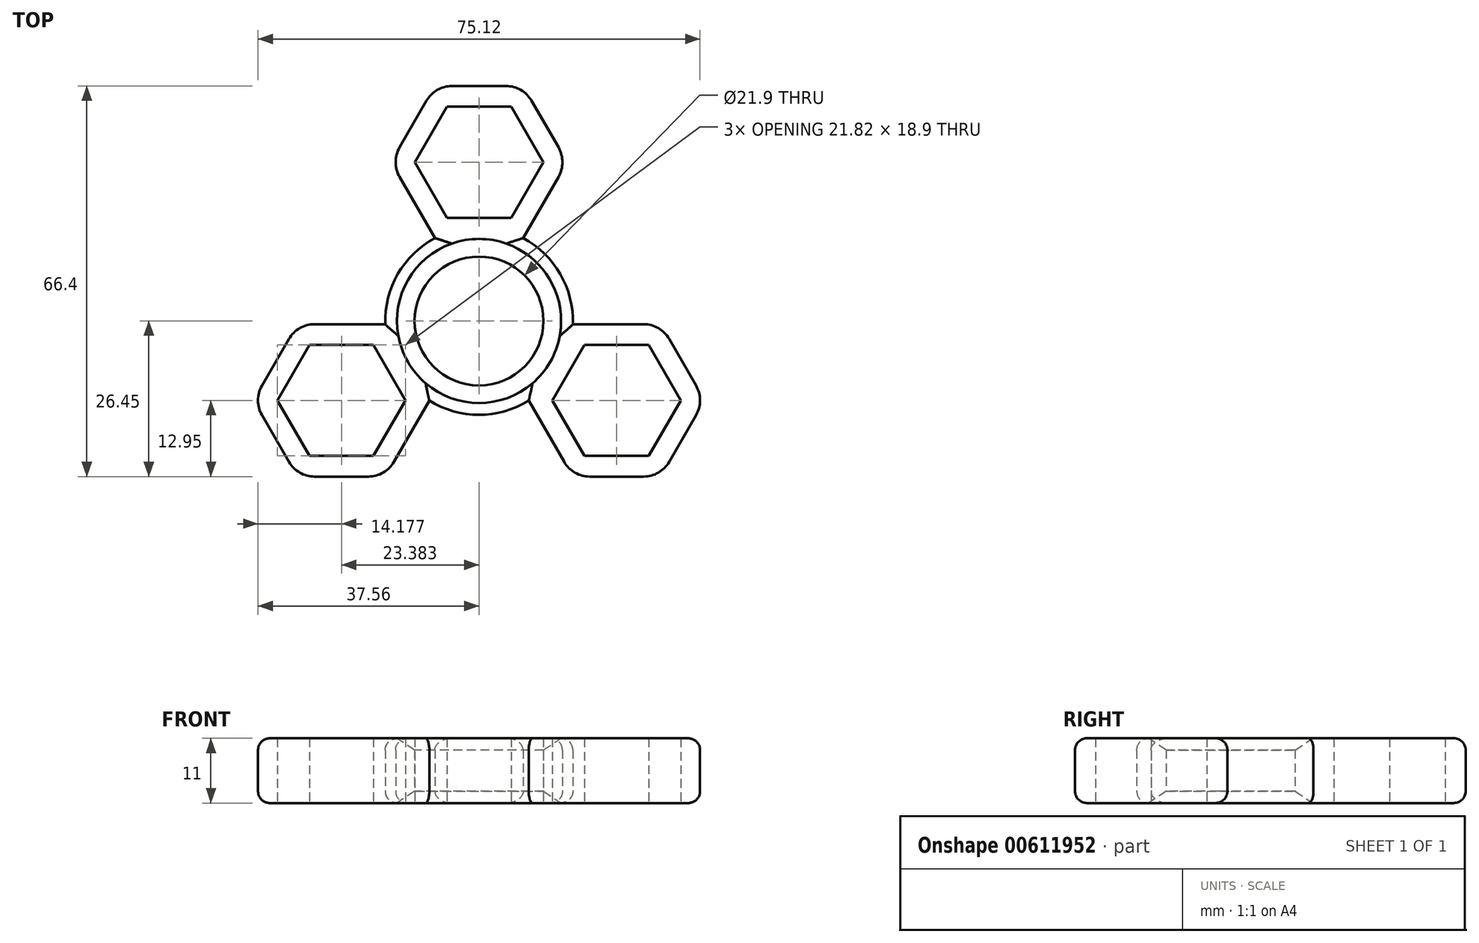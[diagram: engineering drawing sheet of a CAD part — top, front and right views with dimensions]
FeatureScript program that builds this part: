
annotation { "Feature Type Name" : "Feature", "Feature Type Description" : "" }
export const myFeature = defineFeature(function(context is Context, id is Id, definition is map)
    precondition{}
    {
        {
            var Q0;
            Q0=qCreatedBy(makeId("Top.planeOp"),FACE);
            var sketch = newSketch(context, id + "F0", { "sketchPlane" : qUnion([Q0])});
            skCircle(sketch, "E0", {"center": v(0, 0) * mm, "radius": 10.95 * mm});
            skCircle(sketch, "E1.cCircle", {"center": v(0, 0) * mm, "radius": 13.5 * mm, "construction": true});
            skLineSegment(sketch, "E1.0", {"start": v(0, 27) * mm, "end": v(23.38, -13.5) * mm, "construction": true});
            skLineSegment(sketch, "E1.1", {"start": v(23.38, -13.5) * mm, "end": v(-23.38, -13.5) * mm, "construction": true});
            skLineSegment(sketch, "E1.2", {"start": v(-23.38, -13.5) * mm, "end": v(0, 27) * mm, "construction": true});
            skPoint(sketch, "E1.0.midPoint", {"position": v(11.7, 6.75) * mm});
            skLineSegment(sketch, "E2", {"start": v(0, 0) * mm, "end": v(-23.38, -13.5) * mm, "construction": true});
            skLineSegment(sketch, "E3", {"start": v(0, 0) * mm, "end": v(23.38, -13.5) * mm, "construction": true});
            skLineSegment(sketch, "E4", {"start": v(0, 0) * mm, "end": v(0, 27) * mm, "construction": true});
            skCircle(sketch, "E5.cCircle", {"center": v(0, 27) * mm, "radius": 9.45 * mm, "construction": true});
            skLineSegment(sketch, "E5.0", {"start": v(-5.46, 36.45) * mm, "end": v(5.46, 36.45) * mm});
            skLineSegment(sketch, "E5.1", {"start": v(5.46, 36.45) * mm, "end": v(10.91, 27) * mm});
            skLineSegment(sketch, "E5.2", {"start": v(10.91, 27) * mm, "end": v(5.46, 17.55) * mm});
            skLineSegment(sketch, "E5.3", {"start": v(5.46, 17.55) * mm, "end": v(-5.46, 17.55) * mm});
            skLineSegment(sketch, "E5.4", {"start": v(-5.46, 17.55) * mm, "end": v(-10.91, 27) * mm});
            skLineSegment(sketch, "E5.5", {"start": v(-10.91, 27) * mm, "end": v(-5.46, 36.45) * mm});
            skPoint(sketch, "E5.0.midPoint", {"position": v(0, 36.45) * mm});
            skCircle(sketch, "E6.cCircle", {"center": v(23.38, -13.5) * mm, "radius": 9.45 * mm, "construction": true});
            skLineSegment(sketch, "E6.0", {"start": v(34.3, -13.5) * mm, "end": v(28.84, -22.95) * mm});
            skLineSegment(sketch, "E6.1", {"start": v(28.84, -22.95) * mm, "end": v(17.93, -22.95) * mm});
            skLineSegment(sketch, "E6.2", {"start": v(17.93, -22.95) * mm, "end": v(12.47, -13.5) * mm});
            skLineSegment(sketch, "E6.3", {"start": v(12.47, -13.5) * mm, "end": v(17.93, -4.05) * mm});
            skLineSegment(sketch, "E6.4", {"start": v(17.93, -4.05) * mm, "end": v(28.84, -4.05) * mm});
            skLineSegment(sketch, "E6.5", {"start": v(28.84, -4.05) * mm, "end": v(34.3, -13.5) * mm});
            skPoint(sketch, "E6.0.midPoint", {"position": v(31.57, -18.22) * mm});
            skCircle(sketch, "E7.cCircle", {"center": v(-23.38, -13.5) * mm, "radius": 9.45 * mm, "construction": true});
            skLineSegment(sketch, "E7.0", {"start": v(-28.84, -22.95) * mm, "end": v(-34.3, -13.5) * mm});
            skLineSegment(sketch, "E7.1", {"start": v(-34.3, -13.5) * mm, "end": v(-28.84, -4.05) * mm});
            skLineSegment(sketch, "E7.2", {"start": v(-28.84, -4.05) * mm, "end": v(-17.93, -4.05) * mm});
            skLineSegment(sketch, "E7.3", {"start": v(-17.93, -4.05) * mm, "end": v(-12.47, -13.5) * mm});
            skLineSegment(sketch, "E7.4", {"start": v(-12.47, -13.5) * mm, "end": v(-17.93, -22.95) * mm});
            skLineSegment(sketch, "E7.5", {"start": v(-17.93, -22.95) * mm, "end": v(-28.84, -22.95) * mm});
            skPoint(sketch, "E7.0.midPoint", {"position": v(-31.57, -18.22) * mm});
            skLineSegment(sketch, "E8.0", {"start": v(-14.95, 27) * mm, "end": v(-7.48, 39.95) * mm});
            skLineSegment(sketch, "E8.1", {"start": v(7.48, 39.95) * mm, "end": v(14.95, 27) * mm});
            skLineSegment(sketch, "E8.2", {"start": v(14.95, 27) * mm, "end": v(7.48, 14.05) * mm});
            skLineSegment(sketch, "E8.3", {"start": v(-7.48, 39.95) * mm, "end": v(7.48, 39.95) * mm});
            skLineSegment(sketch, "E8.4", {"start": v(7.48, 14.05) * mm, "end": v(-7.48, 14.05) * mm});
            skLineSegment(sketch, "E8.5", {"start": v(-7.48, 14.05) * mm, "end": v(-14.95, 27) * mm});
            skLineSegment(sketch, "E9.0", {"start": v(8.43, -13.5) * mm, "end": v(15.9, -0.55) * mm});
            skLineSegment(sketch, "E9.1", {"start": v(30.86, -0.55) * mm, "end": v(38.34, -13.5) * mm});
            skLineSegment(sketch, "E9.2", {"start": v(38.34, -13.5) * mm, "end": v(30.86, -26.45) * mm});
            skLineSegment(sketch, "E9.3", {"start": v(15.9, -0.55) * mm, "end": v(30.86, -0.55) * mm});
            skLineSegment(sketch, "E9.4", {"start": v(30.86, -26.45) * mm, "end": v(15.9, -26.45) * mm});
            skLineSegment(sketch, "E9.5", {"start": v(15.9, -26.45) * mm, "end": v(8.43, -13.5) * mm});
            skLineSegment(sketch, "E10.0", {"start": v(-38.34, -13.5) * mm, "end": v(-30.86, -0.55) * mm});
            skLineSegment(sketch, "E10.1", {"start": v(-15.9, -0.55) * mm, "end": v(-8.43, -13.5) * mm});
            skLineSegment(sketch, "E10.2", {"start": v(-8.43, -13.5) * mm, "end": v(-15.9, -26.45) * mm});
            skLineSegment(sketch, "E10.3", {"start": v(-30.86, -0.55) * mm, "end": v(-15.9, -0.55) * mm});
            skLineSegment(sketch, "E10.4", {"start": v(-15.9, -26.45) * mm, "end": v(-30.86, -26.45) * mm});
            skLineSegment(sketch, "E10.5", {"start": v(-30.86, -26.45) * mm, "end": v(-38.34, -13.5) * mm});
            skCircle(sketch, "E11.0", {"center": v(0, 0) * mm, "radius": 15.95 * mm});
            skSolve(sketch);
        }
        {
            var Q0;
            Q0 = qSketchRegion(id + "F0", true);
            extrude(context, id + "F1", {"entities" : qUnion([Q0]), "depth" : 11 * mm, "offsetDistance" : 25 * mm});
        }
        {
            var Q0;
            Q0=makeQuery(id+"F1.opExtrude","CAP_EDGE",EDGE,{"disambiguationData":[OSD([sQuery(id+"F0.wireOp",EDGE,"E8.5")])],"isStart":true});
            var Q1;
            {var subQ0=sQuery(id+"F0.wireOp",EDGE,"E11.0");Q1=makeQuery(id+"F1.opExtrude","CAP_EDGE",EDGE,{"disambiguationData":[OSD([subQ0]),TDD([makeQuery(id+"F0.imprint","IMPRINT",EDGE,{"disambiguationData":[TD([[makeQuery(id+"F0.imprint","INTERSECT",VERTEX,{"derivedFrom":[sQuery(id+"F0.wireOp",EDGE,"E8.5"),subQ0]}),-1.0]])],"derivedFrom":subQ0})])],"isStart":true});}
            var Q2;
            Q2=makeQuery(id+"F1.opExtrude","CAP_EDGE",EDGE,{"disambiguationData":[OSD([sQuery(id+"F0.wireOp",EDGE,"E10.3")])],"isStart":true});
            var Q3;
            Q3=makeQuery(id+"F1.opExtrude","CAP_EDGE",EDGE,{"disambiguationData":[OSD([sQuery(id+"F0.wireOp",EDGE,"E10.0")])],"isStart":true});
            var Q4;
            Q4=makeQuery(id+"F1.opExtrude","CAP_EDGE",EDGE,{"disambiguationData":[OSD([sQuery(id+"F0.wireOp",EDGE,"E10.5")])],"isStart":true});
            var Q5;
            Q5=makeQuery(id+"F1.opExtrude","CAP_EDGE",EDGE,{"disambiguationData":[OSD([sQuery(id+"F0.wireOp",EDGE,"E10.4")])],"isStart":true});
            var Q6;
            Q6=makeQuery(id+"F1.opExtrude","CAP_EDGE",EDGE,{"disambiguationData":[OSD([sQuery(id+"F0.wireOp",EDGE,"E10.2")])],"isStart":true});
            var Q7;
            {var subQ0=sQuery(id+"F0.wireOp",EDGE,"E11.0");Q7=makeQuery(id+"F1.opExtrude","CAP_EDGE",EDGE,{"disambiguationData":[OSD([subQ0]),TDD([makeQuery(id+"F0.imprint","IMPRINT",EDGE,{"disambiguationData":[TD([[makeQuery(id+"F0.imprint","INTERSECT",VERTEX,{"derivedFrom":[sQuery(id+"F0.wireOp",EDGE,"E9.5"),subQ0]}),1.0]])],"derivedFrom":subQ0})])],"isStart":true});}
            var Q8;
            Q8=makeQuery(id+"F1.opExtrude","CAP_EDGE",EDGE,{"disambiguationData":[OSD([sQuery(id+"F0.wireOp",EDGE,"E9.4")])],"isStart":true});
            var Q9;
            Q9=makeQuery(id+"F1.opExtrude","CAP_EDGE",EDGE,{"disambiguationData":[OSD([sQuery(id+"F0.wireOp",EDGE,"E9.2")])],"isStart":true});
            var Q10;
            Q10=makeQuery(id+"F1.opExtrude","CAP_EDGE",EDGE,{"disambiguationData":[OSD([sQuery(id+"F0.wireOp",EDGE,"E9.1")])],"isStart":true});
            var Q11;
            Q11=makeQuery(id+"F1.opExtrude","CAP_EDGE",EDGE,{"disambiguationData":[OSD([sQuery(id+"F0.wireOp",EDGE,"E9.3")])],"isStart":true});
            var Q12;
            {var subQ0=sQuery(id+"F0.wireOp",EDGE,"E11.0");Q12=makeQuery(id+"F1.opExtrude","CAP_EDGE",EDGE,{"disambiguationData":[OSD([subQ0]),TDD([makeQuery(id+"F0.imprint","IMPRINT",EDGE,{"disambiguationData":[TD([[makeQuery(id+"F0.imprint","INTERSECT",VERTEX,{"derivedFrom":[sQuery(id+"F0.wireOp",EDGE,"E8.2"),subQ0]}),1.0]])],"derivedFrom":subQ0})])],"isStart":true});}
            var Q13;
            Q13=makeQuery(id+"F1.opExtrude","CAP_EDGE",EDGE,{"disambiguationData":[OSD([sQuery(id+"F0.wireOp",EDGE,"E8.2")])],"isStart":true});
            var Q14;
            Q14=makeQuery(id+"F1.opExtrude","CAP_EDGE",EDGE,{"disambiguationData":[OSD([sQuery(id+"F0.wireOp",EDGE,"E8.1")])],"isStart":true});
            var Q15;
            Q15=makeQuery(id+"F1.opExtrude","CAP_EDGE",EDGE,{"disambiguationData":[OSD([sQuery(id+"F0.wireOp",EDGE,"E8.3")])],"isStart":true});
            var Q16;
            Q16=makeQuery(id+"F1.opExtrude","CAP_EDGE",EDGE,{"disambiguationData":[OSD([sQuery(id+"F0.wireOp",EDGE,"E8.0")])],"isStart":true});
            var Q17;
            Q17=makeQuery(id+"F1.opExtrude","CAP_EDGE",EDGE,{"disambiguationData":[OSD([sQuery(id+"F0.wireOp",EDGE,"E9.4")])],"isStart":false});
            var Q18;
            {var subQ0=sQuery(id+"F0.wireOp",EDGE,"E11.0");Q18=makeQuery(id+"F1.opExtrude","CAP_EDGE",EDGE,{"disambiguationData":[OSD([subQ0]),TDD([makeQuery(id+"F0.imprint","IMPRINT",EDGE,{"disambiguationData":[TD([[makeQuery(id+"F0.imprint","INTERSECT",VERTEX,{"derivedFrom":[sQuery(id+"F0.wireOp",EDGE,"E9.5"),subQ0]}),1.0]])],"derivedFrom":subQ0})])],"isStart":false});}
            var Q19;
            Q19=makeQuery(id+"F1.opExtrude","CAP_EDGE",EDGE,{"disambiguationData":[OSD([sQuery(id+"F0.wireOp",EDGE,"E9.5")])],"isStart":false});
            var Q20;
            Q20=makeQuery(id+"F1.opExtrude","CAP_EDGE",EDGE,{"disambiguationData":[OSD([sQuery(id+"F0.wireOp",EDGE,"E10.2")])],"isStart":false});
            var Q21;
            Q21=makeQuery(id+"F1.opExtrude","CAP_EDGE",EDGE,{"disambiguationData":[OSD([sQuery(id+"F0.wireOp",EDGE,"E10.4")])],"isStart":false});
            var Q22;
            Q22=makeQuery(id+"F1.opExtrude","CAP_EDGE",EDGE,{"disambiguationData":[OSD([sQuery(id+"F0.wireOp",EDGE,"E10.5")])],"isStart":false});
            var Q23;
            Q23=makeQuery(id+"F1.opExtrude","CAP_EDGE",EDGE,{"disambiguationData":[OSD([sQuery(id+"F0.wireOp",EDGE,"E10.0")])],"isStart":false});
            var Q24;
            Q24=makeQuery(id+"F1.opExtrude","CAP_EDGE",EDGE,{"disambiguationData":[OSD([sQuery(id+"F0.wireOp",EDGE,"E10.3")])],"isStart":false});
            var Q25;
            {var subQ0=sQuery(id+"F0.wireOp",EDGE,"E11.0");Q25=makeQuery(id+"F1.opExtrude","CAP_EDGE",EDGE,{"disambiguationData":[OSD([subQ0]),TDD([makeQuery(id+"F0.imprint","IMPRINT",EDGE,{"disambiguationData":[TD([[makeQuery(id+"F0.imprint","INTERSECT",VERTEX,{"derivedFrom":[sQuery(id+"F0.wireOp",EDGE,"E8.5"),subQ0]}),-1.0]])],"derivedFrom":subQ0})])],"isStart":false});}
            var Q26;
            Q26=makeQuery(id+"F1.opExtrude","CAP_EDGE",EDGE,{"disambiguationData":[OSD([sQuery(id+"F0.wireOp",EDGE,"E8.5")])],"isStart":false});
            var Q27;
            Q27=makeQuery(id+"F1.opExtrude","CAP_EDGE",EDGE,{"disambiguationData":[OSD([sQuery(id+"F0.wireOp",EDGE,"E8.0")])],"isStart":false});
            var Q28;
            Q28=makeQuery(id+"F1.opExtrude","CAP_EDGE",EDGE,{"disambiguationData":[OSD([sQuery(id+"F0.wireOp",EDGE,"E8.3")])],"isStart":false});
            var Q29;
            Q29=makeQuery(id+"F1.opExtrude","CAP_EDGE",EDGE,{"disambiguationData":[OSD([sQuery(id+"F0.wireOp",EDGE,"E8.1")])],"isStart":false});
            var Q30;
            Q30=makeQuery(id+"F1.opExtrude","CAP_EDGE",EDGE,{"disambiguationData":[OSD([sQuery(id+"F0.wireOp",EDGE,"E8.2")])],"isStart":false});
            var Q31;
            {var subQ0=sQuery(id+"F0.wireOp",EDGE,"E11.0");Q31=makeQuery(id+"F1.opExtrude","CAP_EDGE",EDGE,{"disambiguationData":[OSD([subQ0]),TDD([makeQuery(id+"F0.imprint","IMPRINT",EDGE,{"disambiguationData":[TD([[makeQuery(id+"F0.imprint","INTERSECT",VERTEX,{"derivedFrom":[sQuery(id+"F0.wireOp",EDGE,"E8.2"),subQ0]}),1.0]])],"derivedFrom":subQ0})])],"isStart":false});}
            var Q32;
            Q32=makeQuery(id+"F1.opExtrude","CAP_EDGE",EDGE,{"disambiguationData":[OSD([sQuery(id+"F0.wireOp",EDGE,"E9.3")])],"isStart":false});
            var Q33;
            Q33=makeQuery(id+"F1.opExtrude","CAP_EDGE",EDGE,{"disambiguationData":[OSD([sQuery(id+"F0.wireOp",EDGE,"E9.1")])],"isStart":false});
            var Q34;
            Q34=makeQuery(id+"F1.opExtrude","CAP_EDGE",EDGE,{"disambiguationData":[OSD([sQuery(id+"F0.wireOp",EDGE,"E9.2")])],"isStart":false});
            var Q35;
            Q35=makeQuery(id+"F1.opExtrude","CAP_EDGE",EDGE,{"disambiguationData":[OSD([sQuery(id+"F0.wireOp",EDGE,"E9.5")])],"isStart":true});
            fillet(context, id + "F2", {"entities" : qUnion([Q0, Q1, Q2, Q3, Q4, Q5, Q6, Q7, Q8, Q9, Q10, Q11, Q12, Q13, Q14, Q15, Q16, Q17, Q18, Q19, Q20, Q21, Q22, Q23, Q24, Q25, Q26, Q27, Q28, Q29, Q30, Q31, Q32, Q33, Q34, Q35]), "radius" : 2 * mm, "tangentPropagation" : true, "allowEdgeOverflow" : false});
        }
        {
            var Q0;
            Q0=makeQuery(id+"F1.opExtrude","SWEPT_EDGE",EDGE,{"disambiguationData":[OSD([sQuery(id+"F0.wireOp",EDGE,"E9.4"),sQuery(id+"F0.wireOp",EDGE,"E9.5")])]});
            var Q1;
            Q1=makeQuery(id+"F1.opExtrude","SWEPT_EDGE",EDGE,{"disambiguationData":[OSD([sQuery(id+"F0.wireOp",EDGE,"E9.2"),sQuery(id+"F0.wireOp",EDGE,"E9.4")])]});
            var Q2;
            Q2=makeQuery(id+"F1.opExtrude","SWEPT_EDGE",EDGE,{"disambiguationData":[OSD([sQuery(id+"F0.wireOp",EDGE,"E9.1"),sQuery(id+"F0.wireOp",EDGE,"E9.2")])]});
            var Q3;
            Q3=makeQuery(id+"F1.opExtrude","SWEPT_EDGE",EDGE,{"disambiguationData":[OSD([sQuery(id+"F0.wireOp",EDGE,"E9.1"),sQuery(id+"F0.wireOp",EDGE,"E9.3")])]});
            var Q4;
            Q4=makeQuery(id+"F1.opExtrude","SWEPT_EDGE",EDGE,{"disambiguationData":[OSD([sQuery(id+"F0.wireOp",EDGE,"E8.1"),sQuery(id+"F0.wireOp",EDGE,"E8.2")])]});
            var Q5;
            Q5=makeQuery(id+"F1.opExtrude","SWEPT_EDGE",EDGE,{"disambiguationData":[OSD([sQuery(id+"F0.wireOp",EDGE,"E8.1"),sQuery(id+"F0.wireOp",EDGE,"E8.3")])]});
            var Q6;
            Q6=makeQuery(id+"F1.opExtrude","SWEPT_EDGE",EDGE,{"disambiguationData":[OSD([sQuery(id+"F0.wireOp",EDGE,"E8.0"),sQuery(id+"F0.wireOp",EDGE,"E8.3")])]});
            var Q7;
            Q7=makeQuery(id+"F1.opExtrude","SWEPT_EDGE",EDGE,{"disambiguationData":[OSD([sQuery(id+"F0.wireOp",EDGE,"E8.0"),sQuery(id+"F0.wireOp",EDGE,"E8.5")])]});
            var Q8;
            Q8=makeQuery(id+"F1.opExtrude","SWEPT_EDGE",EDGE,{"disambiguationData":[OSD([sQuery(id+"F0.wireOp",EDGE,"E10.0"),sQuery(id+"F0.wireOp",EDGE,"E10.3")])]});
            var Q9;
            Q9=makeQuery(id+"F1.opExtrude","SWEPT_EDGE",EDGE,{"disambiguationData":[OSD([sQuery(id+"F0.wireOp",EDGE,"E10.0"),sQuery(id+"F0.wireOp",EDGE,"E10.5")])]});
            var Q10;
            Q10=makeQuery(id+"F1.opExtrude","SWEPT_EDGE",EDGE,{"disambiguationData":[OSD([sQuery(id+"F0.wireOp",EDGE,"E10.4"),sQuery(id+"F0.wireOp",EDGE,"E10.5")])]});
            var Q11;
            Q11=makeQuery(id+"F1.opExtrude","SWEPT_EDGE",EDGE,{"disambiguationData":[OSD([sQuery(id+"F0.wireOp",EDGE,"E10.2"),sQuery(id+"F0.wireOp",EDGE,"E10.4")])]});
            fillet(context, id + "F3", {"entities" : qUnion([Q0, Q1, Q2, Q3, Q4, Q5, Q6, Q7, Q8, Q9, Q10, Q11]), "radius" : 5 * mm, "tangentPropagation" : true, "allowEdgeOverflow" : false});
        }
        {
            var Q0;
            Q0=makeQuery(id+"F1.opExtrude","CAP_EDGE",EDGE,{"disambiguationData":[OSD([sQuery(id+"F0.wireOp",EDGE,"E0")])],"isStart":true});
            var Q1;
            Q1=makeQuery(id+"F1.opExtrude","CAP_EDGE",EDGE,{"disambiguationData":[OSD([sQuery(id+"F0.wireOp",EDGE,"E0")])],"isStart":false});
            chamfer(context, id + "F4", {"entities" : qUnion([Q0, Q1]), "chamferType" : ChamferType.TWO_OFFSETS, "width1" : 3 * mm, "oppositeDirection" : false, "width2" : 2 * mm, "tangentPropagation" : true});
        }
    });
